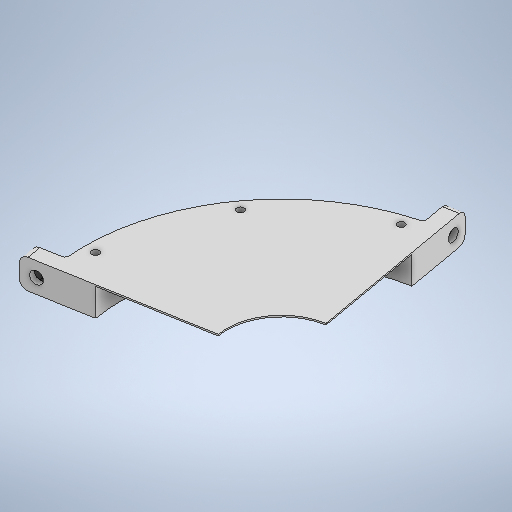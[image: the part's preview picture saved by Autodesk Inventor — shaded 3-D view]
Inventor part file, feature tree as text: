
AUTODESK INVENTOR PART (.ipt)
format: ipt  version: 2025 (Build 290162000, 162)  size: 352,768 bytes
history: native  units: in
note: dims shown in document units (in); Inventor stores cm internally (conversion verified against a paired STEP export)
features: sketch x10, extrude x6, hole x3, fillet x2
ambient origin geometry x8: Origin, YZ Plane, XZ Plane, XY Plane, X Axis, Y Axis, Z Axis, Center Point
bodies: Solid1 (feature_tree)
feature tree (21):
  extrude  "Extrusion1"  Depth=8.6614in
  extrude  "Extrusion2"  Depth=0.7874in
  hole  "Hole1"  [1 undecoded]
  extrude  "Extrusion3"  Depth=0.1969in TaperAngle=360.0deg
  extrude  "Extrusion4"  Depth=5.315in
  fillet  "Fillet1"  Radius=5.315in
  extrude  "Extrusion5"  Depth=0.6871in
  fillet  "Fillet2"  [1 undecoded]
  hole  "Hole2"  [1 undecoded]
  extrude  "Extrusion6"  Depth=0.1969in
  hole  "Hole3"  [1 undecoded]
  sketch  "Sketch1"  dims[d0=10.6299in d1=8.6614in]
  sketch  "Sketch2"  dims[d5=0.0394in d6=0.0in d7=10.0394in]
  sketch  "Sketch3"  dims[d8=0.1969in d9=3.937in d11=360.0deg]
  sketch  "Sketch Circular Pattern1"  dims[d2=0.7874in d3=0.0in d4=2.9528in]
  sketch  "Sketch4"  dims[d13=0.1969in d14=0.2362in d15=0.1575in d16=0.0787in d17=90.0deg d18=0.315in d19=0.8108in d20=10.6299in d21=5.315in]
  sketch  "Sketch5"  dims[d22=0.0687in d23=0.6871in d24=0.0in d25=0.0in]
  sketch  "Sketch6"  dims[d26=0.8858in d27=0.7874in]
  sketch  "Sketch7"  dims[d28=0.7874in d29=0.1969in]
  sketch  "Sketch8"  dims[d30=0.3937in d31=0.0in d32=0.0984in]
  sketch  "Sketch9"  dims[d33=0.8858in d34=0.7874in d35=0.7874in d36=0.1969in d37=0.3937in d38=0.0in d39=0.0984in d40=0.3937in d41=0.3937in d42=0.3228in d43=0.2362in d44=0.5197in d45=0.2362in d46=90.0deg d47=0.315in d48=0.8108in d49=0.3937in d50=0.3937in d51=0.5197in d52=0.2362in d53=0.0in d54=0.3937in d55=0.3937in d56=0.3228in d57=0.2362in d58=0.5197in d59=0.2362in d60=90.0deg d61=0.315in d62=0.8108in]
note: 4 required parameter values undecoded (feature->parameter linkage not recoverable at this tier; creation-order binding heuristic only, values carry confidence <= 0.55)
